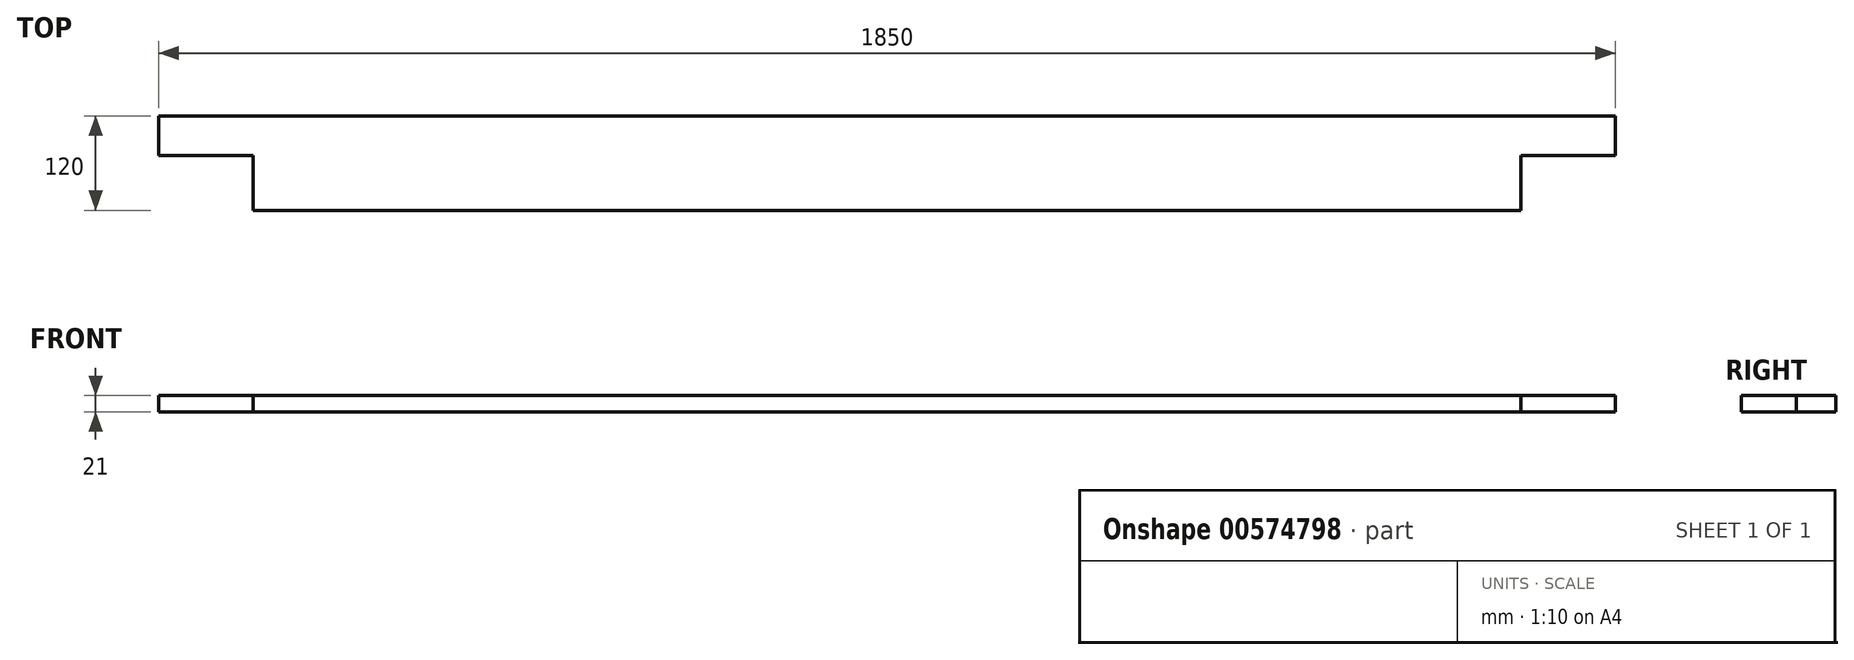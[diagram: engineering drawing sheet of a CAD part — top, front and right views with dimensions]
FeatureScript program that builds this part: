
annotation { "Feature Type Name" : "Feature", "Feature Type Description" : "" }
export const myFeature = defineFeature(function(context is Context, id is Id, definition is map)
    precondition{}
    {
        {
            var Q0;
            Q0=qCreatedBy(makeId("Right.planeOp"),FACE);
            var sketch = newSketch(context, id + "F0", { "sketchPlane" : qUnion([Q0])});
            skLineSegment(sketch, "E0.bottom", {"start": v(-60, -10.5) * mm, "end": v(60, -10.5) * mm});
            skLineSegment(sketch, "E0.top", {"start": v(-60, 10.5) * mm, "end": v(60, 10.5) * mm});
            skLineSegment(sketch, "E0.left", {"start": v(-60, -10.5) * mm, "end": v(-60, 10.5) * mm});
            skLineSegment(sketch, "E0.right", {"start": v(60, -10.5) * mm, "end": v(60, 10.5) * mm});
            skSolve(sketch);
        }
        {
            var Q0;
            Q0=makeQuery(id+"F0.imprint","IMPRINT",FACE,{"disambiguationData":[TD([[makeQuery(id+"F0.imprint","IMPRINT",EDGE,{"derivedFrom":sQuery(id+"F0.wireOp",EDGE,"E0.bottom")}),1.0]])]});
            extrude(context, id + "F1", {"entities" : qUnion([Q0]), "depth" : (2000 - 150) * mm, "offsetDistance" : 25 * mm});
        }
        {
            var Q0;
            Q0=makeQuery(id+"F1.opExtrude","SWEPT_FACE",FACE,{"disambiguationData":[OSD([sQuery(id+"F0.wireOp",EDGE,"E0.top")])]});
            var sketch = newSketch(context, id + "F2", { "sketchPlane" : qUnion([Q0])});
            skLineSegment(sketch, "E1.bottom", {"start": v(1730, -60) * mm, "end": v(1850, -60) * mm});
            skLineSegment(sketch, "E1.top", {"start": v(1730, 10) * mm, "end": v(1850, 10) * mm});
            skLineSegment(sketch, "E1.left", {"start": v(1850, -60) * mm, "end": v(1850, 10) * mm});
            skLineSegment(sketch, "E1.right", {"start": v(1730, -60) * mm, "end": v(1730, 10) * mm});
            skLineSegment(sketch, "E2.bottom", {"start": v(0, -60) * mm, "end": v(120, -60) * mm});
            skLineSegment(sketch, "E2.top", {"start": v(0, 10) * mm, "end": v(120, 10) * mm});
            skLineSegment(sketch, "E2.left", {"start": v(0, -60) * mm, "end": v(0, 10) * mm});
            skLineSegment(sketch, "E2.right", {"start": v(120, -60) * mm, "end": v(120, 10) * mm});
            skSolve(sketch);
        }
        {
            var Q0;
            Q0 = qSketchRegion(id + "F2", true);
            extrude(context, id + "F3", {"entities" : qUnion([Q0]), "operationType" : NewBodyOperationType.REMOVE, "oppositeDirection" : true, "depth" : 25 * mm, "offsetDistance" : 25 * mm});
        }
    });
